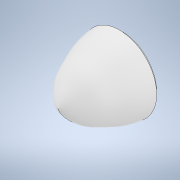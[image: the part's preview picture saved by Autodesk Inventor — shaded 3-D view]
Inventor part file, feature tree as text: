
AUTODESK INVENTOR PART (.ipt)
format: ipt  version: 2020 (Build 240168000, 168)  size: 191,488 bytes
history: native  units: mm
features: revolve x1, sketch x1
ambient origin geometry x8: Origin, YZ Plane, XZ Plane, XY Plane, X Axis, Y Axis, Z Axis, Center Point
bodies: Solid1 (feature_tree)
feature tree (2):
  revolve  "Revolution1"  [1 undecoded]
  sketch  "Sketch1"  dims[d21=90.0deg d25=2.0mm d26=2.0mm d27=2.0mm d29=10.0mm d31=29.0mm d32=48.0mm d33=25.0mm d34=15.0mm d35=27.0mm d11=0.872665mm d12=0.872665mm]
note: 1 required parameter value undecoded (feature->parameter linkage not recoverable at this tier; creation-order binding heuristic only, values carry confidence <= 0.55)
